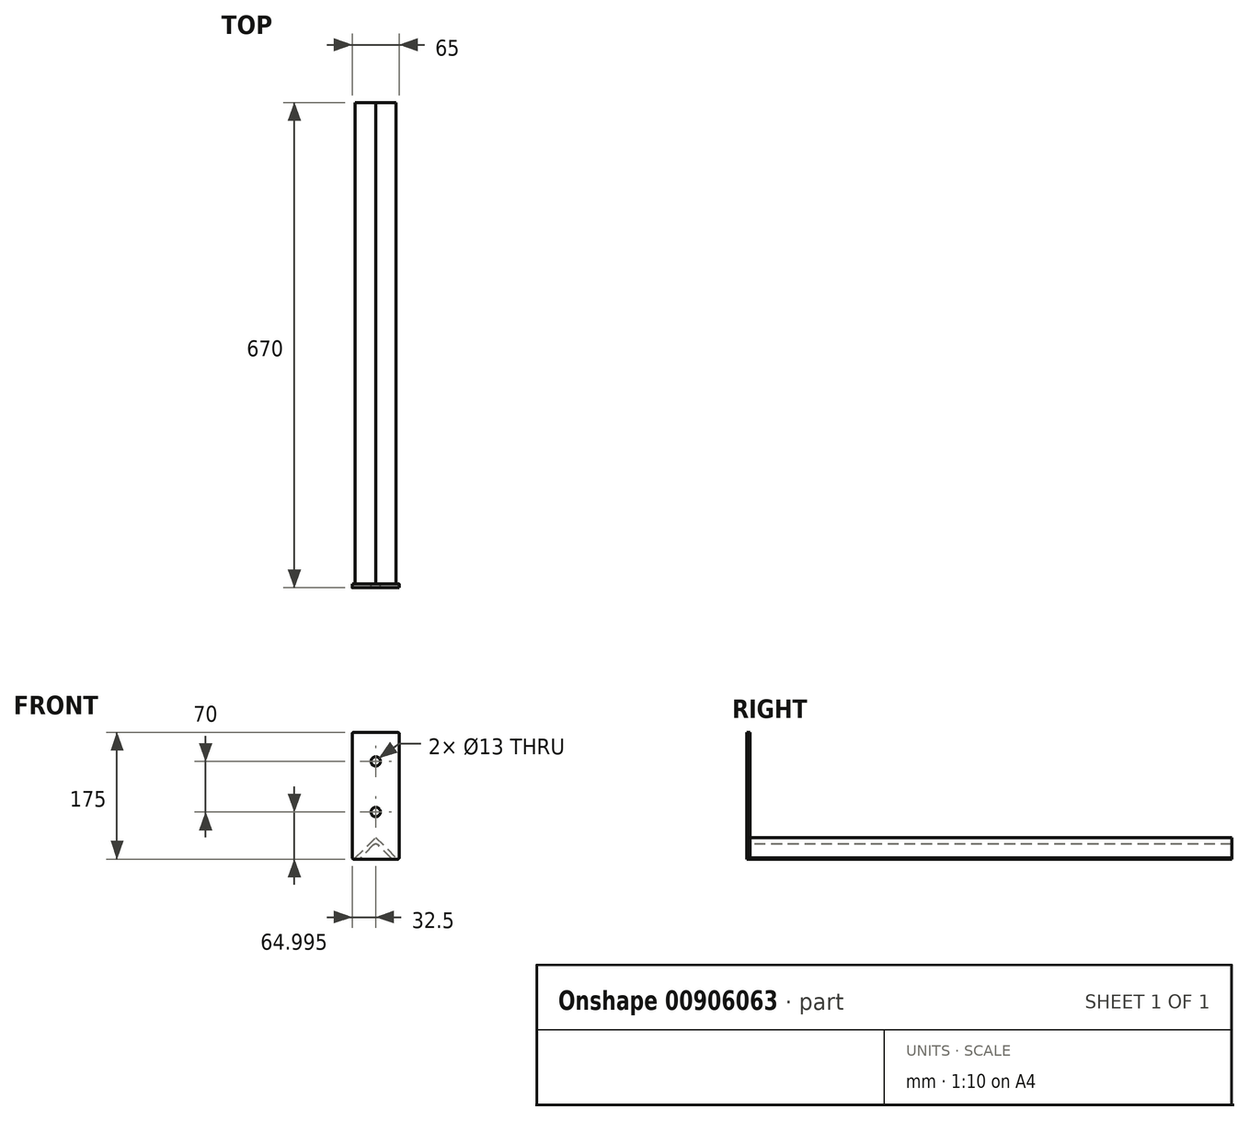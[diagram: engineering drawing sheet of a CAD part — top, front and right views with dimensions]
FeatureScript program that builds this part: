
annotation { "Feature Type Name" : "Feature", "Feature Type Description" : "" }
export const myFeature = defineFeature(function(context is Context, id is Id, definition is map)
    precondition{}
    {
        {
            var Q0;
            Q0=qCreatedBy(makeId("Front.planeOp"),FACE);
            var sketch = newSketch(context, id + "F0", { "sketchPlane" : qUnion([Q0])});
            skLineSegment(sketch, "E0", {"start": v(-28.28, 0) * mm, "end": v(0, 28.28) * mm});
            skLineSegment(sketch, "E1", {"start": v(0, 28.28) * mm, "end": v(28.28, 0) * mm});
            skLineSegment(sketch, "E2", {"start": v(28.28, 0) * mm, "end": v(24.75, -3.54) * mm});
            skLineSegment(sketch, "E3", {"start": v(24.75, -3.54) * mm, "end": v(0, 21.21) * mm});
            skLineSegment(sketch, "E4", {"start": v(0, 21.21) * mm, "end": v(-24.75, -3.54) * mm});
            skLineSegment(sketch, "E5", {"start": v(-24.75, -3.54) * mm, "end": v(-28.28, 0) * mm});
            skSolve(sketch);
        }
        {
            var Q0;
            Q0=makeQuery(id+"F0.imprint","IMPRINT",FACE,{"disambiguationData":[TD([[makeQuery(id+"F0.imprint","IMPRINT",EDGE,{"derivedFrom":sQuery(id+"F0.wireOp",EDGE,"E0")}),-1.0]])]});
            extrude(context, id + "F1", {"entities" : qUnion([Q0]), "depth" : 332.5 * mm, "offsetDistance" : 25 * mm, "hasSecondDirection" : true, "secondDirectionOppositeDirection" : true, "secondDirectionDepth" : 332.5 * mm});
        }
        {
            var Q0;
            Q0=makeQuery(id+"F1.opExtrude","SWEPT_EDGE",EDGE,{"disambiguationData":[OSD([sQuery(id+"F0.wireOp",EDGE,"E2"),sQuery(id+"F0.wireOp",EDGE,"E3")])]});
            var Q1;
            Q1=makeQuery(id+"F1.opExtrude","SWEPT_EDGE",EDGE,{"disambiguationData":[OSD([sQuery(id+"F0.wireOp",EDGE,"E3"),sQuery(id+"F0.wireOp",EDGE,"E4")])]});
            var Q2;
            Q2=makeQuery(id+"F1.opExtrude","SWEPT_EDGE",EDGE,{"disambiguationData":[OSD([sQuery(id+"F0.wireOp",EDGE,"E4"),sQuery(id+"F0.wireOp",EDGE,"E5")])]});
            fillet(context, id + "F2", {"entities" : qUnion([Q0, Q1, Q2]), "radius" : 5 * mm, "tangentPropagation" : true, "allowEdgeOverflow" : false});
        }
        {
            var Q0;
            Q0=makeQuery(id+"F1.opExtrude","CAP_FACE",FACE,{"disambiguationData":[OSD([sQuery(id+"F0.wireOp",EDGE,"E0"),sQuery(id+"F0.wireOp",EDGE,"E1"),sQuery(id+"F0.wireOp",EDGE,"E2"),sQuery(id+"F0.wireOp",EDGE,"E3"),sQuery(id+"F0.wireOp",EDGE,"E4"),sQuery(id+"F0.wireOp",EDGE,"E5")])],"isStart":false});
            var sketch = newSketch(context, id + "F3", { "sketchPlane" : qUnion([Q0])});
            skLineSegment(sketch, "E6.bottom", {"start": v(-32.5, -1.46) * mm, "end": v(32.5, -1.46) * mm});
            skLineSegment(sketch, "E6.top", {"start": v(-32.5, 173.54) * mm, "end": v(32.5, 173.54) * mm});
            skLineSegment(sketch, "E6.left", {"start": v(-32.5, -1.46) * mm, "end": v(-32.5, 173.54) * mm});
            skLineSegment(sketch, "E6.right", {"start": v(32.5, -1.46) * mm, "end": v(32.5, 173.54) * mm});
            skLineSegment(sketch, "E7", {"start": v(0, 173.54) * mm, "end": v(0, -1.46) * mm, "construction": true});
            skSolve(sketch);
        }
        {
            var Q0;
            Q0 = qSketchRegion(id + "F3", true);
            extrude(context, id + "F4", {"entities" : qUnion([Q0]), "operationType" : NewBodyOperationType.ADD, "depth" : 5 * mm, "offsetDistance" : 25 * mm});
        }
        {
            var Q0;
            Q0=makeQuery(id+"F4.opExtrude","SWEPT_EDGE",EDGE,{"disambiguationData":[OSD([sQuery(id+"F3.wireOp",EDGE,"E6.top"),sQuery(id+"F3.wireOp",EDGE,"E6.right")])]});
            var Q1;
            Q1=makeQuery(id+"F4.opExtrude","SWEPT_EDGE",EDGE,{"disambiguationData":[OSD([sQuery(id+"F3.wireOp",EDGE,"E6.bottom"),sQuery(id+"F3.wireOp",EDGE,"E6.right")])]});
            var Q2;
            Q2=makeQuery(id+"F4.opExtrude","SWEPT_EDGE",EDGE,{"disambiguationData":[OSD([sQuery(id+"F3.wireOp",EDGE,"E6.top"),sQuery(id+"F3.wireOp",EDGE,"E6.left")])]});
            var Q3;
            Q3=makeQuery(id+"F4.opExtrude","SWEPT_EDGE",EDGE,{"disambiguationData":[OSD([sQuery(id+"F3.wireOp",EDGE,"E6.bottom"),sQuery(id+"F3.wireOp",EDGE,"E6.left")])]});
            fillet(context, id + "F5", {"entities" : qUnion([Q0, Q1, Q2, Q3]), "radius" : 2 * mm, "tangentPropagation" : true, "allowEdgeOverflow" : false});
        }
        {
            var Q0;
            Q0=makeQuery(id+"F4.opExtrude","CAP_FACE",FACE,{"disambiguationData":[OSD([sQuery(id+"F3.wireOp",EDGE,"E6.bottom"),sQuery(id+"F3.wireOp",EDGE,"E6.top"),sQuery(id+"F3.wireOp",EDGE,"E6.left"),sQuery(id+"F3.wireOp",EDGE,"E6.right")])],"isStart":false});
            var sketch = newSketch(context, id + "F6", { "sketchPlane" : qUnion([Q0])});
            skPoint(sketch, "E8", {"position": v(0, 63.54) * mm});
            skPoint(sketch, "E9", {"position": v(0, 133.54) * mm});
            skSolve(sketch);
        }
        {
            var Q0;
            Q0=sQuery(id+"F6.wireOp",VERTEX,"13e51a3d-816a-42ab-8cc7-a8cf678fa35f");
            var Q1;
            Q1=sQuery(id+"F6.wireOp",VERTEX,"3d219333-495a-44af-89cc-2b73a013f21b");
            var Q2;
            Q2=sQuery(id+"F6.wireOp",VERTEX,"E8");
            var Q3;
            Q3=sQuery(id+"F6.wireOp",VERTEX,"E9");
            var Q4;
            Q4=makeQuery(id+"F1.opExtrude","SWEPT_BODY",BODY,{"disambiguationData":[OSD([sQuery(id+"F0.wireOp",EDGE,"E0"),sQuery(id+"F0.wireOp",EDGE,"E1"),sQuery(id+"F0.wireOp",EDGE,"E2"),sQuery(id+"F0.wireOp",EDGE,"E3"),sQuery(id+"F0.wireOp",EDGE,"E4"),sQuery(id+"F0.wireOp",EDGE,"E5")])]});
            hole(context, id + "F7", {"style" : HoleStyle.SIMPLE, "endStyle" : HoleEndStyle.THROUGH, "holeDiameter" : 13 * mm, "majorDiameter" : 5 * mm, "isTappedThrough" : true, "tappedDepth" : 12 * mm, "tapClearance" : 3, "locations" : qUnion([Q0, Q1, Q2, Q3]), "scope" : qUnion([Q4]), "startStyle" : HoleStartStyle.PART});
        }
    });
